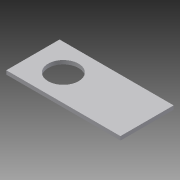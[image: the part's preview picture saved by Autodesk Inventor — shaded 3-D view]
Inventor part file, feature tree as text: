
AUTODESK INVENTOR PART (.ipt)
format: ipt  version: 2013 (Build 170138000, 138)  size: 72,704 bytes
history: native  units: mm
features: extrude x1, hole x1, sketch x1
ambient origin geometry x8: Origin, YZ Plane, XZ Plane, XY Plane, X Axis, Y Axis, Z Axis, Center Point
bodies: Volumenkörper1 (feature_tree)
feature tree (3):
  extrude  "Extrusion1"  Depth=7.0mm
  hole  "Bohrung1"  [1 undecoded]
  sketch  "Skizze1"  dims[d0=15.0mm d1=7.0mm d2=0.5mm d3=0.0mm d4=4.0mm d5=3.5mm d6=4.0mm d7=6.0mm d8=4.0mm d9=2.0mm d10=90.0deg d11=8.0mm d12=20.594885mm]
note: 1 required parameter value undecoded (feature->parameter linkage not recoverable at this tier; creation-order binding heuristic only, values carry confidence <= 0.55)
